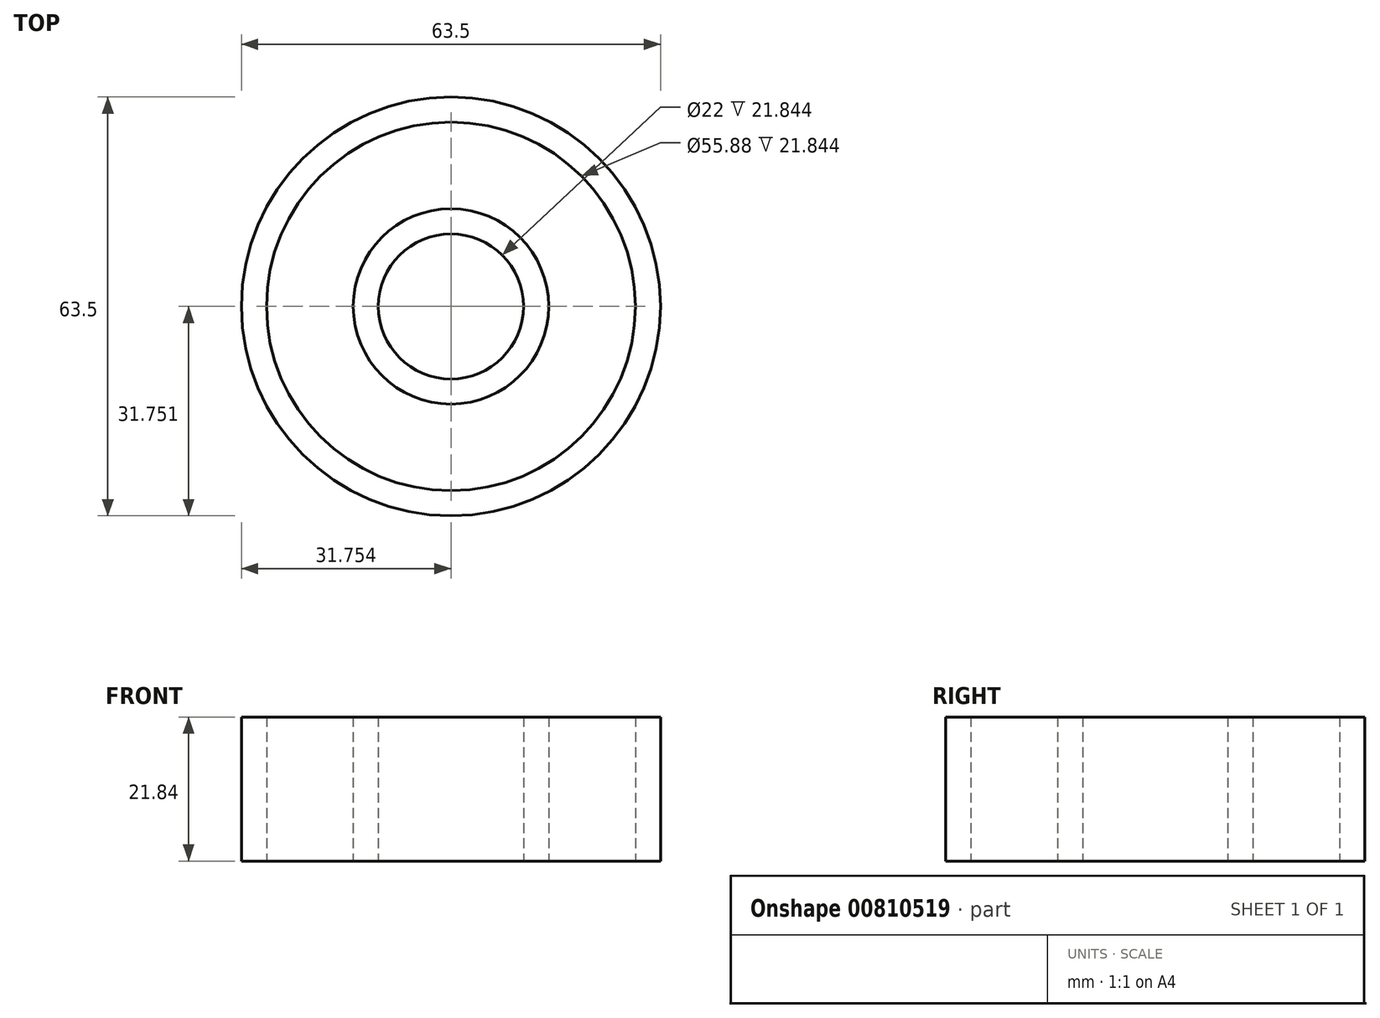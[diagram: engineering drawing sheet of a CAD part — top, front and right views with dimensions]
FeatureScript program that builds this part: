
annotation { "Feature Type Name" : "Feature", "Feature Type Description" : "" }
export const myFeature = defineFeature(function(context is Context, id is Id, definition is map)
    precondition{}
    {
        {
            var Q0;
            Q0=qCreatedBy(makeId("Top.planeOp"),FACE);
            var sketch = newSketch(context, id + "F0", { "sketchPlane" : qUnion([Q0])});
            skCircle(sketch, "E0", {"center": v(-65.67, -42.84) * mm, "radius": 11 * mm});
            skCircle(sketch, "E1", {"center": v(-65.67, -42.84) * mm, "radius": 31.75 * mm});
            skCircle(sketch, "E2", {"center": v(-65.67, -42.84) * mm, "radius": 14.8 * mm});
            skCircle(sketch, "E3", {"center": v(-65.67, -42.84) * mm, "radius": 27.94 * mm});
            skSolve(sketch);
        }
        {
            var Q0;
            Q0 = qSketchRegion(id + "FDRwM4pofDAS9tY_0", true);
            var Q1;
            Q1=makeQuery(id+"F0.imprint","IMPRINT",FACE,{"disambiguationData":[TD([[makeQuery(id+"F0.imprint","IMPRINT",EDGE,{"derivedFrom":sQuery(id+"F0.wireOp",EDGE,"E1")}),1.0]])]});
            var Q2;
            Q2=makeQuery(id+"F0.imprint","IMPRINT",FACE,{"disambiguationData":[TD([[makeQuery(id+"F0.imprint","IMPRINT",EDGE,{"derivedFrom":sQuery(id+"F0.wireOp",EDGE,"E0")}),-1.0]])]});
            extrude(context, id + "F1", {"entities" : qUnion([Q0, Q1, Q2]), "depth" : 21.84 * mm, "offsetDistance" : 25.4 * mm});
        }
    });
